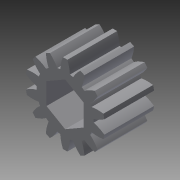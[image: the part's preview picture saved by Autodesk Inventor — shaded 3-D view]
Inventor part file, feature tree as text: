
AUTODESK INVENTOR PART (.ipt)
format: ipt  version: 2013 (Build 170138000, 138)  size: 184,320 bytes
history: native  units: in
note: dims shown in document units (in); Inventor stores cm internally (conversion verified against a paired STEP export)
features: other x2, extrude x2, sketch x2, imported_body x1
ambient origin geometry x8: Origin, YZ Plane, XZ Plane, XY Plane, X Axis, Y Axis, Z Axis, Center Point
feature tree (7):
  other  "Toughbox_d09"
  other  "Toughbox_d091"
  extrude  "Extrusion1"  Depth=0.5in TaperAngle=0.0deg
  extrude  "Extrusion2"  [1 undecoded]
  imported_body  "Base1"
  sketch  "Sketch1"  dims[d0=0.375in d1=0.5in d2=0.0in]
  sketch  "Sketch2"  dims[d3=0.5in d4=0.0in]
note: 1 required parameter value undecoded (feature->parameter linkage not recoverable at this tier; creation-order binding heuristic only, values carry confidence <= 0.55)
